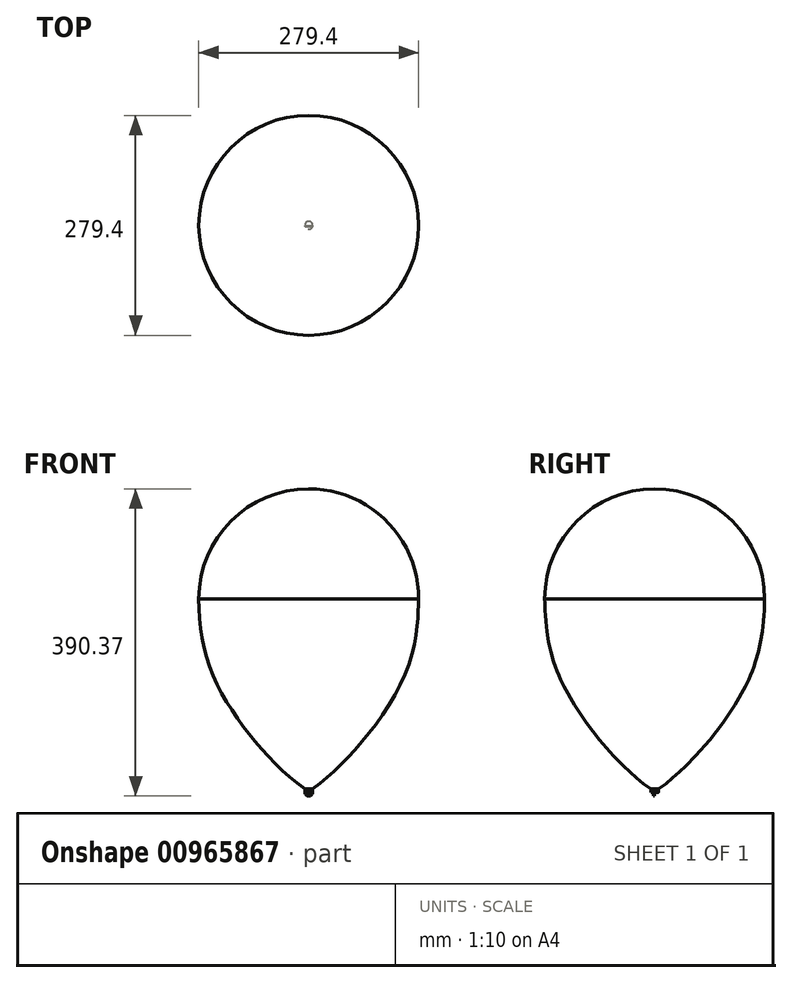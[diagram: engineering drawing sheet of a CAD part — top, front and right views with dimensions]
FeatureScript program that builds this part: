
annotation { "Feature Type Name" : "Feature", "Feature Type Description" : "" }
export const myFeature = defineFeature(function(context is Context, id is Id, definition is map)
    precondition{}
    {
        {
            var Q0;
            Q0=qCreatedBy(makeId("Front.planeOp"),FACE);
            var sketch = newSketch(context, id + "F0", { "sketchPlane" : qUnion([Q0])});
            skArc(sketch, "E0", {"start": v(0, 139.7) * mm, "mid": v(-98.78, 98.78) * mm, "end": v(-139.7, 0) * mm});
            skArc(sketch, "E1", {"start": v(0, 139.45) * mm, "mid": v(-98.6, 98.6) * mm, "end": v(-139.45, 0) * mm});
            skLineSegment(sketch, "E2", {"start": v(139.45, 0) * mm, "end": v(139.7, 0) * mm});
            skLineSegment(sketch, "E3", {"start": v(-139.45, 0) * mm, "end": v(-139.7, 0) * mm});
            skFitSpline(sketch, "E4", {"points": [v(-139.45, 0) * mm, v(-126.98, -82.3) * mm, v(-88.5, -154.3) * mm, v(-41.94, -209.23) * mm, v(0, -245) * mm], "startDerivative": vector(12.95, -304.22) * mm, "endDerivative": vector(163.17, -102.13) * mm});
            skLineSegment(sketch, "E5", {"start": v(0, 139.45) * mm, "end": v(0, 139.7) * mm});
            skPoint(sketch, "E5.endSnap0", {"position": v(0, 139.45) * mm});
            skFitSpline(sketch, "E6", {"points": [v(-139.7, 0) * mm, v(-138.3, -27.16) * mm, v(-127.5, -82.3) * mm, v(-88.93, -154.3) * mm, v(-42.45, -209.23) * mm, v(0, -245.36) * mm], "startDerivative": vector(6.11, -190.08) * mm, "endDerivative": vector(228.99, -159.32) * mm});
            skLineSegment(sketch, "E7", {"start": v(0, -245) * mm, "end": v(0, -245.36) * mm});
            skLineSegment(sketch, "E8", {"start": v(0, 139.7) * mm, "end": v(0, -245) * mm});
            skSolve(sketch);
        }
        {
            var Q0;
            {var subQ0=sQuery(id+"F0.wireOp",EDGE,"E0");Q0=makeQuery(id+"F0.imprint","IMPRINT",FACE,{"disambiguationData":[TD([[makeQuery(id+"F0.imprint","IMPRINT",EDGE,{"derivedFrom":subQ0}),1.0]])]});}
            var Q1;
            {var subQ0=sQuery(id+"F0.wireOp",EDGE,"E3");Q1=makeQuery(id+"F0.imprint","IMPRINT",FACE,{"disambiguationData":[TD([[makeQuery(id+"F0.imprint","IMPRINT",EDGE,{"derivedFrom":subQ0}),1.0]])]});}
            var Q2;
            {var subQ0=sQuery(id+"F0.wireOp",EDGE,"E6");var subQ1=sQuery(id+"F0.wireOp",EDGE,"E4");var subQ2=makeQuery(id+"F0.imprint","INTERSECT",VERTEX,{"disambiguationData":[OD(0.0)],"derivedFrom":[subQ1,subQ0]});Q2=makeQuery(id+"F0.imprint","IMPRINT",FACE,{"disambiguationData":[TD([[makeQuery(id+"F0.imprint","IMPRINT",EDGE,{"disambiguationData":[TD([[subQ2,-1.0]])],"derivedFrom":subQ1}),1.0]])]});}
            var Q3;
            {var subQ0=sQuery(id+"F0.wireOp",EDGE,"E7");Q3=makeQuery(id+"F0.imprint","IMPRINT",FACE,{"disambiguationData":[TD([[makeQuery(id+"F0.imprint","IMPRINT",EDGE,{"derivedFrom":subQ0}),-1.0]])]});}
            var Q4;
            Q4=sQuery(id+"F0.wireOp",EDGE,"E8");
            revolve(context, id + "F1", {"surfaceOperationType" : NewSurfaceOperationType.NEW, "entities" : qUnion([Q0, Q1, Q2, Q3]), "axis" : qUnion([Q4]), "revolveType" : RevolveType.FULL});
        }
        {
            var Q0;
            Q0=qCreatedBy(makeId("Top.planeOp"),FACE);
            cPlane(context, id + "F2", {"entities" : qUnion([Q0]), "cplaneType" : CPlaneType.OFFSET, "offset" : 241.3 * mm, "oppositeDirection" : true, "width" : 152.4 * mm, "height" : 152.4 * mm});
        }
        {
            var Q0;
            Q0=qCreatedBy(id+"F2.planeOp",FACE);
            var sketch = newSketch(context, id + "F3", { "sketchPlane" : qUnion([Q0])});
            skCircle(sketch, "E9", {"center": v(0, 0) * mm, "radius": 5.03 * mm});
            skSolve(sketch);
        }
        {
            var Q0;
            Q0 = qSketchRegion(id + "F3", true);
            extrude(context, id + "F4", {"entities" : qUnion([Q0]), "operationType" : NewBodyOperationType.ADD, "depth" : 25.4 * mm, "offsetDistance" : 25.4 * mm});
        }
        {
            var Q0;
            Q0 = qSketchRegion(id + "F3", true);
            extrude(context, id + "F5", {"entities" : qUnion([Q0]), "operationType" : NewBodyOperationType.ADD, "oppositeDirection" : true, "depth" : 4.32 * mm, "offsetDistance" : 25.4 * mm});
        }
        {
            var Q0;
            Q0=qCreatedBy(makeId("Front.planeOp"),FACE);
            var sketch = newSketch(context, id + "F6", { "sketchPlane" : qUnion([Q0])});
            skArc(sketch, "E10", {"start": v(-3.25, -245.63) * mm, "mid": v(0.02, -248.89) * mm, "end": v(3.25, -245.6) * mm});
            skArc(sketch, "E11", {"start": v(-5.03, -245.64) * mm, "mid": v(0.03, -250.67) * mm, "end": v(5.03, -245.59) * mm});
            skLineSegment(sketch, "E12", {"start": v(5.03, -245.59) * mm, "end": v(-5.03, -245.64) * mm});
            skSolve(sketch);
        }
        {
            var Q0;
            {var subQ0=sQuery(id+"F6.wireOp",EDGE,"E10");Q0=makeQuery(id+"F6.imprint","IMPRINT",FACE,{"disambiguationData":[TD([[makeQuery(id+"F6.imprint","IMPRINT",EDGE,{"derivedFrom":subQ0}),-1.0]])]});}
            extrude(context, id + "F7", {"entities" : qUnion([Q0]), "operationType" : NewBodyOperationType.ADD, "depth" : 1.27 * mm, "offsetDistance" : 25.4 * mm});
        }
    });
